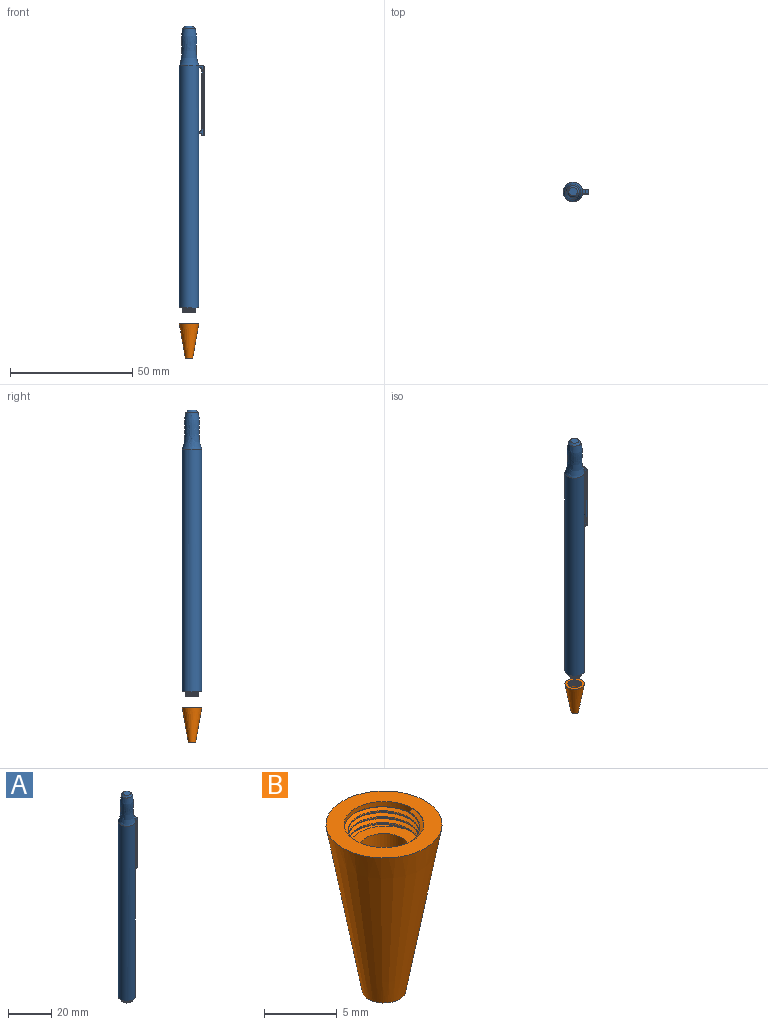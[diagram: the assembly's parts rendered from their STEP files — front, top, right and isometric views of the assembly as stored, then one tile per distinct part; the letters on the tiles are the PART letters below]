
ASSEMBLY  parts=2 mates=1
PART A: 97 faces, bbox 10.6x8.2x117.7 mm
  f0: cylinder r=4mm len=99.3mm, axis (0,0,-1), area 2493.7mm2, adj f4,f5,f16,f23,f24,f73,f75,f85
  f1: cylinder r=1.75mm len=116.3mm, axis (0,0,-1), area 1278.8mm2, adj f2,f8
  f2: plane 5.41x5.41mm, normal (0,0,-1), area 11.9mm2, adj f1,f3,f10,f11,f12
  f3: cylinder r=2.75mm len=5.5mm, axis (0,0,-1), area 9.4mm2, adj f2,f4,f9,f10,f11
  f4: plane 8x8mm, normal (0,0,-1), area 26.5mm2, adj f0,f3
  f5: revolved ~15x8mm, area 294mm2, adj f0,f6,f13
  f6: cone r=2.5mm half-angle=36.9deg, axis (0,0,-1), area 16.7mm2, adj f5,f7
  f7: plane 3.5x3.5mm, normal (0,0,1), area 9.6mm2, adj f6
  f8: plane 3.5x3.5mm, normal (0,0,-1), area 9.6mm2, adj f1
  f9: plane 0.4x0.3mm, normal (0,-1,0), area 0.1mm2, adj f3,f10,f11,f12
  f10: bspline ~6.35x5.5mm, area 17.3mm2, adj f2,f3,f9,f12
  f11: bspline ~6.35x5.5mm, area 19.8mm2, adj f2,f3,f9,f12
  f12: bspline ~4.97x4.97mm, area 5.8mm2, adj f2,f9,f10,f11
  f13: plane 1.8x1.3mm, normal (0,0,1), area 2.2mm2, adj f5,f15,f75,f87
  f14: plane 27.9x1.8mm, normal (1,0,0), area 48.7mm2, adj f15,f22,f27,f28,f29,f30,f31,f32
  f15: cylinder r=1mm len=1.8mm, axis (0,1,0), area 2.8mm2, adj f13,f14,f77,f89
  f16: plane 1.8x0.3mm, normal (0,0,-1), area 0.4mm2, adj f0,f17,f73,f85
  f17: cylinder r=1mm len=1.8mm, axis (0,1,0), area 2.8mm2, adj f16,f18,f74,f86
  f18: plane 24.09x1.8mm, normal (-1,0,0), area 43.4mm2, adj f17,f25,f76,f88
  f19: cylinder r=0.5mm len=1.8mm, axis (0,1,0), area 2.2mm2, adj f25,f26,f80,f92
  f20: cylinder r=0.1mm len=1.8mm, axis (0,1,0), area 0.3mm2, adj f21,f26,f84,f96
  f21: plane 1.8x0.8mm, normal (0,0,-1), area 1.4mm2, adj f20,f22,f83,f95
  f22: cylinder r=0.1mm len=1.8mm, axis (0,1,0), area 0.3mm2, adj f14,f21,f81,f93
  f23: plane 28.8x2.23mm, normal (0,-1,0), area 25.4mm2, adj f0,f73,f74,f75,f76,f77,f78,f79
  f24: plane 28.8x2.23mm, normal (0,1,0), area 25.4mm2, adj f0,f85,f86,f87,f88,f89,f90,f91
  f25: cylinder r=1mm len=1.8mm, axis (0,1,0), area 2.2mm2, adj f18,f19,f78,f90
  f26: cylinder r=1mm len=1.8mm, axis (0,-1,0), area 2.2mm2, adj f19,f20,f82,f94
  f27: plane 0.85x0.8mm, normal (0,0.69,-0.73), area 0.2mm2, adj f14,f28,f71,f72
  f28: plane 0.2x0.15mm, normal (0,-0.95,-0.32), area 0mm2, adj f14,f27,f29,f72
  f29: plane 0.2x0.15mm, normal (0,0,-1), area 0mm2, adj f14,f28,f30,f72
  f30: plane 0.5x0.2mm, normal (0,1,0), area 0.1mm2, adj f14,f29,f31,f72
  f31: plane 0.2x0.15mm, normal (0,0,1), area 0mm2, adj f14,f30,f32,f72
  f32: plane 0.2x0.15mm, normal (0,-0.95,0.32), area 0mm2, adj f14,f31,f33,f72
  f33: plane 1.1x0.2mm, normal (0,0,1), area 0.2mm2, adj f14,f32,f34,f72
  f34: plane 0.2x0.15mm, normal (0,0.95,0.32), area 0mm2, adj f14,f33,f35,f72
  f35: plane 0.2x0.15mm, normal (0,0,1), area 0mm2, adj f14,f34,f36,f72
  f36: plane 0.5x0.2mm, normal (0,-1,0), area 0.1mm2, adj f14,f35,f37,f72
  f37: plane 0.2x0.15mm, normal (0,0,-1), area 0mm2, adj f14,f36,f38,f72
  f38: plane 0.2x0.15mm, normal (0,0.95,-0.32), area 0mm2, adj f14,f37,f39,f72
  f39: plane 0.85x0.2mm, normal (0,0,-1), area 0.2mm2, adj f14,f38,f40,f72
  f40: plane 0.85x0.8mm, normal (0,-0.69,0.73), area 0.2mm2, adj f14,f39,f41,f72
  f41: plane 0.2x0.15mm, normal (0,0.95,0.32), area 0mm2, adj f14,f40,f42,f72
  f42: plane 0.2x0.15mm, normal (0,0,1), area 0mm2, adj f14,f41,f43,f72
  f43: plane 0.5x0.2mm, normal (0,-1,0), area 0.1mm2, adj f14,f42,f44,f72
  f44: plane 0.2x0.15mm, normal (0,0,-1), area 0mm2, adj f14,f43,f45,f72
  f45: plane 0.2x0.15mm, normal (0,0.95,-0.32), area 0mm2, adj f14,f44,f46,f72
  f46: plane 0.5x0.2mm, normal (0,0,-1), area 0.1mm2, adj f14,f45,f47,f72
  f47: plane 0.45x0.2mm, normal (0,-1,0), area 0.1mm2, adj f14,f46,f48,f72
  f48: plane 0.5x0.35mm, normal (0,-0.57,0.82), area 0.1mm2, adj f14,f47,f49,f72
  f49: plane 0.2x0.15mm, normal (0,0.95,0.32), area 0mm2, adj f14,f48,f50,f72
  f50: plane 0.2x0.15mm, normal (0,0,1), area 0mm2, adj f14,f49,f51,f72
  f51: plane 0.5x0.2mm, normal (0,-1,0), area 0.1mm2, adj f14,f50,f52,f72
  f52: plane 0.2x0.15mm, normal (0,0,-1), area 0mm2, adj f14,f51,f53,f72
  f53: plane 0.2x0.15mm, normal (0,0.95,-0.32), area 0mm2, adj f14,f52,f54,f72
  f54: plane 0.5x0.35mm, normal (0,0.57,-0.82), area 0.1mm2, adj f14,f53,f55,f72
  f55: plane 0.2x0.1mm, normal (0,0.71,-0.71), area 0mm2, adj f14,f54,f56,f72
  f56: plane 0.2x0.1mm, normal (0,-0.71,-0.71), area 0mm2, adj f14,f55,f57,f72
  f57: plane 0.4x0.35mm, normal (0,-0.66,-0.75), area 0.1mm2, adj f14,f56,f58,f72
  f58: plane 0.2x0.15mm, normal (0,-0.95,-0.32), area 0mm2, adj f14,f57,f59,f72
  f59: plane 0.2x0.15mm, normal (0,0,-1), area 0mm2, adj f14,f58,f60,f72
  f60: plane 0.5x0.2mm, normal (0,1,0), area 0.1mm2, adj f14,f59,f61,f72
  f61: plane 0.2x0.15mm, normal (0,0,1), area 0mm2, adj f14,f60,f62,f72
  f62: plane 0.2x0.15mm, normal (0,-0.95,0.32), area 0mm2, adj f14,f61,f63,f72
  f63: plane 0.4x0.35mm, normal (0,0.66,0.75), area 0.1mm2, adj f14,f62,f64,f72
  f64: plane 0.45x0.2mm, normal (0,1,0), area 0.1mm2, adj f14,f63,f65,f72
  f65: plane 0.4x0.2mm, normal (0,0,-1), area 0.1mm2, adj f14,f64,f66,f72
  f66: plane 0.2x0.15mm, normal (0,-0.95,-0.32), area 0mm2, adj f14,f65,f67,f72
  f67: plane 0.2x0.15mm, normal (0,0,-1), area 0mm2, adj f14,f66,f68,f72
  f68: plane 0.5x0.2mm, normal (0,1,0), area 0.1mm2, adj f14,f67,f69,f72
  f69: plane 0.2x0.15mm, normal (0,0,1), area 0mm2, adj f14,f68,f70,f72
  f70: plane 0.2x0.15mm, normal (0,-0.95,0.32), area 0mm2, adj f14,f69,f71,f72
  f71: plane 0.85x0.2mm, normal (0,0,1), area 0.2mm2, adj f14,f27,f70,f72
  f72: plane 2.5x1.5mm, normal (1,0,0), area 1.5mm2, adj f27,f28,f29,f30,f31,f32,f33,f34
  f73: cylinder r=0.1mm len=0.33mm, axis (-1,0,0), area 0mm2, adj f0,f16,f23,f74
  f74: torus R=1.1mm, axis (0,-1,0), area 0.3mm2, adj f17,f23,f73,f76
  f75: cylinder r=0.1mm len=1.33mm, axis (1,0,0), area 0.2mm2, adj f0,f13,f23,f77
  f76: cylinder r=0.1mm len=24.09mm, axis (0,0,1), area 3.8mm2, adj f18,f23,f74,f78
  f77: torus R=0.9mm, axis (0,-1,0), area 0.2mm2, adj f15,f23,f75,f79
  f78: torus R=1.1mm, axis (0,-1,0), area 0.2mm2, adj f23,f25,f76,f80
  f79: cylinder r=0.1mm len=27.9mm, axis (0,0,-1), area 4.4mm2, adj f14,f23,f77,f81
  f80: torus R=0.4mm, axis (0,-1,0), area 0.2mm2, adj f19,f23,f78,f82
  f81: sphere r=0.1mm, area 0mm2, adj f22,f79,f83
  f82: torus R=1.1mm, axis (0,-1,0), area 0.2mm2, adj f23,f26,f80,f84
  f83: cylinder r=0.1mm len=0.8mm, axis (-1,0,0), area 0.1mm2, adj f21,f23,f81,f84
  f84: sphere r=0.1mm, area 0mm2, adj f20,f82,f83
  f85: cylinder r=0.1mm len=0.33mm, axis (1,0,0), area 0mm2, adj f0,f16,f24,f86
  f86: torus R=1.1mm, axis (0,-1,0), area 0.3mm2, adj f17,f24,f85,f88
  f87: cylinder r=0.1mm len=1.33mm, axis (-1,0,0), area 0.2mm2, adj f0,f13,f24,f89
  f88: cylinder r=0.1mm len=24.09mm, axis (0,0,-1), area 3.8mm2, adj f18,f24,f86,f90
  f89: torus R=0.9mm, axis (0,-1,0), area 0.2mm2, adj f15,f24,f87,f91
  f90: torus R=1.1mm, axis (0,-1,0), area 0.2mm2, adj f24,f25,f88,f92
  f91: cylinder r=0.1mm len=27.9mm, axis (0,0,1), area 4.4mm2, adj f14,f24,f89,f93
  f92: torus R=0.4mm, axis (0,-1,0), area 0.2mm2, adj f19,f24,f90,f94
  f93: sphere r=0.1mm, area 0mm2, adj f22,f91,f95
  f94: torus R=1.1mm, axis (0,-1,0), area 0.2mm2, adj f24,f26,f92,f96
  f95: cylinder r=0.1mm len=0.8mm, axis (1,0,0), area 0.1mm2, adj f21,f24,f93,f96
  f96: sphere r=0.1mm, area 0mm2, adj f20,f94,f95
PART B: 13 faces, bbox 8.2x8.2x14.2 mm
  f0: cylinder r=2.75mm len=5.5mm, axis (0,0,-1), area 9.4mm2, adj f1,f7,f8,f10,f11
  f1: plane 5.41x5.41mm, normal (0,0,1), area 11.9mm2, adj f0,f2,f8,f9,f10,f12
  f2: cylinder r=1.75mm len=3.5mm, axis (0,0,-1), area 33mm2, adj f1,f3
  f3: plane 3.5x3.5mm, normal (0,0,1), area 6.5mm2, adj f2,f4
  f4: cylinder r=1mm len=9mm, axis (0,0,-1), area 56.5mm2, adj f3,f5
  f5: plane 3x3mm, normal (0,0,-1), area 3.9mm2, adj f4,f6
  f6: cone r=4mm half-angle=10.1deg, axis (0,0,1), area 245.7mm2, adj f5,f7
  f7: plane 8x8mm, normal (0,0,1), area 26.5mm2, adj f0,f6
  f8: bspline ~6.35x5.5mm, area 1.1mm2, adj f0,f1,f9,f11
  f9: bspline ~6.32x5.47mm, area 18.7mm2, adj f1,f8,f11,f12
  f10: bspline ~6.35x5.5mm, area 17.3mm2, adj f0,f1,f11,f12
  f11: plane 0.4x0.3mm, normal (0,1,0), area 0.1mm2, adj f0,f8,f9,f10,f12
  f12: bspline ~4.96x4.96mm, area 5.8mm2, adj f1,f9,f10,f11
PLACE A t=(-0.28,-0.95,-56.27)mm fixed
PLACE B rot(axis=(0,0,-1),120.8deg) t=(-0.28,-0.95,-53.67)mm
MATE cylindrical B.f6 <-> A.f0  axis (0,0,-1) through (-0.28,-0.95,-64.9)mm
